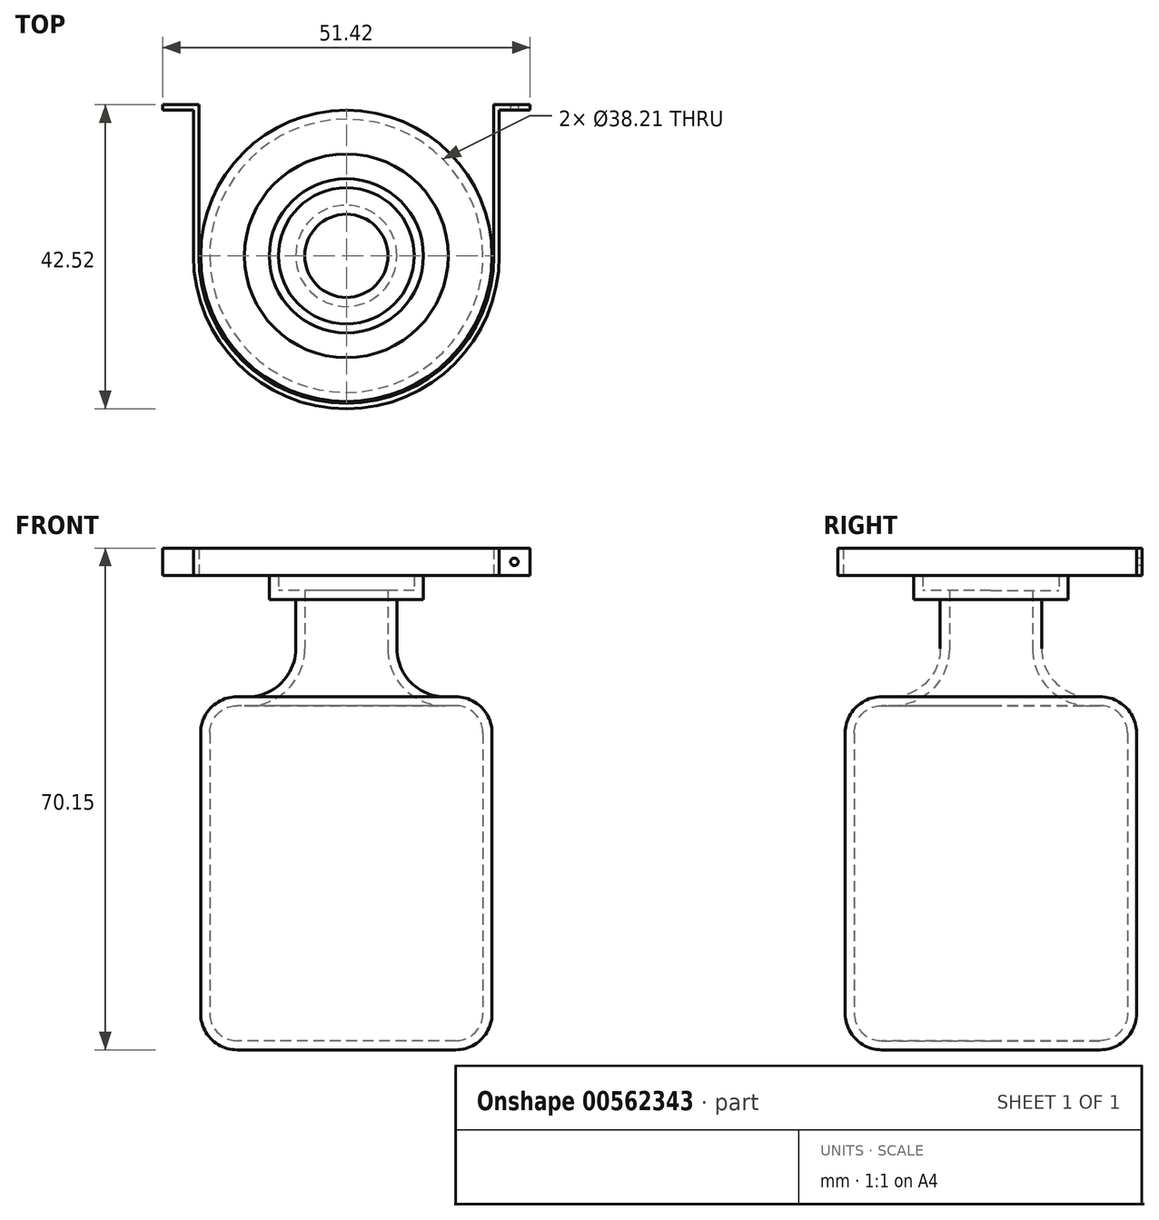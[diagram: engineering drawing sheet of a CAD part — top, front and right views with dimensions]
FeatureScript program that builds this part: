
annotation { "Feature Type Name" : "Feature", "Feature Type Description" : "" }
export const myFeature = defineFeature(function(context is Context, id is Id, definition is map)
    precondition{}
    {
        {
            var Q0;
            Q0=qCreatedBy(makeId("Front.planeOp"),FACE);
            var sketch = newSketch(context, id + "F0", { "sketchPlane" : qUnion([Q0])});
            skLineSegment(sketch, "E0", {"start": v(0, 0) * mm, "end": v(-10.78, 0) * mm});
            skLineSegment(sketch, "E1", {"start": v(-10.78, 0) * mm, "end": v(-10.78, -3.37) * mm});
            skLineSegment(sketch, "E2", {"start": v(-10.78, -3.37) * mm, "end": v(-7.08, -3.37) * mm});
            skLineSegment(sketch, "E3", {"start": v(-7.08, -3.37) * mm, "end": v(-7.08, -10.24) * mm});
            skLineSegment(sketch, "E4", {"start": v(-20.37, -16.95) * mm, "end": v(-14.24, -16.95) * mm});
            skArc(sketch, "E5", {"start": v(-7.08, -10.24) * mm, "mid": v(-9.2, -15.14) * mm, "end": v(-14.24, -16.95) * mm});
            skLineSegment(sketch, "E6", {"start": v(-20.37, -16.95) * mm, "end": v(-20.37, -66.34) * mm});
            skLineSegment(sketch, "E7", {"start": v(-20.37, -66.34) * mm, "end": v(0, -66.34) * mm});
            skLineSegment(sketch, "E8", {"start": v(0, -66.34) * mm, "end": v(0, 0) * mm});
            skSolve(sketch);
        }
        {
            var Q0;
            Q0 = qSketchRegion(id + "F0", true);
            var Q1;
            Q1=sQuery(id+"F0.wireOp",EDGE,"E8");
            revolve(context, id + "F1", {"entities" : qUnion([Q0]), "axis" : qUnion([Q1]), "revolveType" : RevolveType.FULL});
        }
        {
            var Q0;
            Q0=makeQuery(id+"F1.opRevolve","SWEPT_EDGE",EDGE,{"disambiguationData":[OSD([sQuery(id+"F0.wireOp",EDGE,"E4"),sQuery(id+"F0.wireOp",EDGE,"E6")])]});
            fillet(context, id + "F2", {"entities" : qUnion([Q0]), "radius" : 5.08 * mm, "tangentPropagation" : true, "allowEdgeOverflow" : false});
        }
        {
            var Q0;
            Q0=makeQuery(id+"F1.opRevolve","SWEPT_EDGE",EDGE,{"disambiguationData":[OSD([sQuery(id+"F0.wireOp",EDGE,"E6"),sQuery(id+"F0.wireOp",EDGE,"E7")])]});
            fillet(context, id + "F3", {"entities" : qUnion([Q0]), "radius" : 5.08 * mm, "tangentPropagation" : true, "allowEdgeOverflow" : false});
        }
        {
            var Q0;
            Q0=makeQuery(id+"F1.opRevolve","SWEPT_FACE",FACE,{"disambiguationData":[OSD([sQuery(id+"F0.wireOp",EDGE,"E0")])]});
            shell(context, id + "F4", {"entities" : qUnion([Q0]), "thickness" : 1.27 * mm});
        }
        {
            var Q0;
            Q0=qCreatedBy(makeId("Top.planeOp"),FACE);
            var sketch = newSketch(context, id + "F5", { "sketchPlane" : qUnion([Q0])});
            skArc(sketch, "E9.0", {"start": v(-20.63, 0) * mm, "mid": v(0, -20.63) * mm, "end": v(20.63, 0) * mm});
            skArc(sketch, "E10.0", {"start": v(-21.39, 0) * mm, "mid": v(0, -21.39) * mm, "end": v(21.39, 0) * mm});
            skLineSegment(sketch, "E11", {"start": v(-21.39, 0) * mm, "end": v(-21.39, 20.37) * mm});
            skLineSegment(sketch, "E12", {"start": v(-20.63, 0) * mm, "end": v(-20.63, 21.13) * mm});
            skLineSegment(sketch, "E13", {"start": v(21.39, 0) * mm, "end": v(21.39, 20.37) * mm});
            skLineSegment(sketch, "E14", {"start": v(20.63, 0) * mm, "end": v(20.63, 21.13) * mm});
            skLineSegment(sketch, "E15", {"start": v(20.63, 21.13) * mm, "end": v(25.7, 21.13) * mm});
            skLineSegment(sketch, "E16", {"start": v(25.7, 21.13) * mm, "end": v(25.7, 20.37) * mm});
            skLineSegment(sketch, "E17", {"start": v(25.7, 20.37) * mm, "end": v(21.39, 20.37) * mm});
            skLineSegment(sketch, "E18", {"start": v(-20.63, 21.13) * mm, "end": v(-25.7, 21.13) * mm});
            skLineSegment(sketch, "E19", {"start": v(-25.7, 21.13) * mm, "end": v(-25.7, 20.37) * mm});
            skLineSegment(sketch, "E20", {"start": v(-25.7, 20.37) * mm, "end": v(-21.39, 20.37) * mm});
            skLineSegment(sketch, "E21", {"start": v(-20.63, 21.13) * mm, "end": v(20.63, 21.13) * mm, "construction": true});
            skSolve(sketch);
        }
        {
            var Q0;
            Q0 = qSketchRegion(id + "F5", true);
            extrude(context, id + "F6", {"entities" : qUnion([Q0]), "depth" : 3.8 * mm, "offsetDistance" : 25.4 * mm});
        }
        {
            var Q0;
            Q0=makeQuery(id+"F6.opExtrude","SWEPT_FACE",FACE,{"disambiguationData":[OSD([sQuery(id+"F5.wireOp",EDGE,"E17")])]});
            var sketch = newSketch(context, id + "F7", { "sketchPlane" : qUnion([Q0])});
            skCircle(sketch, "E22", {"center": v(23.5, 1.9) * mm, "radius": 0.53 * mm});
            skSolve(sketch);
        }
        {
            var Q0;
            Q0=makeQuery(id+"F7.imprint","IMPRINT",FACE,{"disambiguationData":[TD([[makeQuery(id+"F7.imprint","IMPRINT",EDGE,{"derivedFrom":sQuery(id+"F7.wireOp",EDGE,"E22")}),1.0]])]});
            extrude(context, id + "F8", {"entities" : qUnion([Q0]), "operationType" : NewBodyOperationType.REMOVE, "endBound" : BoundingType.THROUGH_ALL, "oppositeDirection" : true, "depth" : 25.4 * mm, "offsetDistance" : 25.4 * mm});
        }
    });
